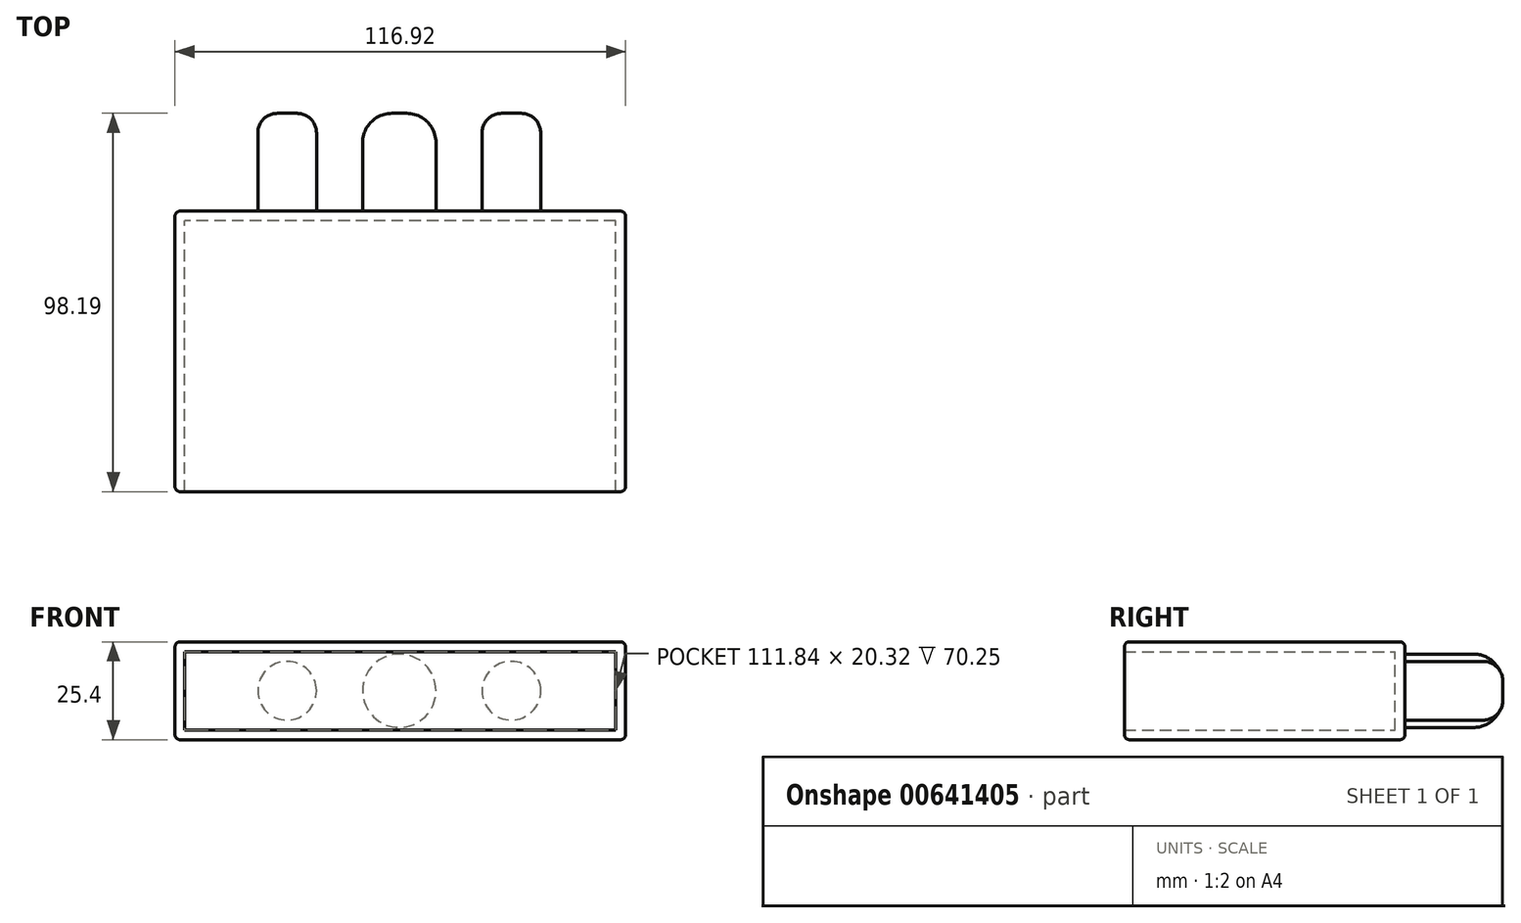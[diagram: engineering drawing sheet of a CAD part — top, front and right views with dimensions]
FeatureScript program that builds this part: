
annotation { "Feature Type Name" : "Feature", "Feature Type Description" : "" }
export const myFeature = defineFeature(function(context is Context, id is Id, definition is map)
    precondition{}
    {
        {
            var Q0;
            Q0=qCreatedBy(makeId("Top.planeOp"),FACE);
            var sketch = newSketch(context, id + "F0", { "sketchPlane" : qUnion([Q0])});
            skLineSegment(sketch, "E0.bottom", {"start": v(-58.2, 31.02) * mm, "end": v(58.72, 31.02) * mm});
            skLineSegment(sketch, "E0.top", {"start": v(-58.2, -41.77) * mm, "end": v(58.72, -41.77) * mm});
            skLineSegment(sketch, "E0.left", {"start": v(-58.2, 31.02) * mm, "end": v(-58.2, -41.77) * mm});
            skLineSegment(sketch, "E0.right", {"start": v(58.72, 31.02) * mm, "end": v(58.72, -41.77) * mm});
            skSolve(sketch);
        }
        {
            var Q0;
            Q0 = qSketchRegion(id + "F0", true);
            extrude(context, id + "F1", {"entities" : qUnion([Q0]), "depth" : 25.4 * mm, "offsetDistance" : 25.4 * mm});
        }
        {
            var Q0;
            Q0=makeQuery(id+"F1.opExtrude","SWEPT_FACE",FACE,{"disambiguationData":[OSD([sQuery(id+"F0.wireOp",EDGE,"E0.bottom")])]});
            var sketch = newSketch(context, id + "F2", { "sketchPlane" : qUnion([Q0])});
            skCircle(sketch, "E1", {"center": v(0, 12.7) * mm, "radius": 9.53 * mm});
            skLineSegment(sketch, "E2", {"start": v(0, 12.7) * mm, "end": v(0, 0) * mm, "construction": true});
            skLineSegment(sketch, "E3", {"start": v(0, 12.7) * mm, "end": v(58.2, 12.7) * mm, "construction": true});
            skCircle(sketch, "E4", {"center": v(29.1, 12.7) * mm, "radius": 7.62 * mm});
            skCircle(sketch, "E5.MirrorC", {"center": v(-29.1, 12.7) * mm, "radius": 7.62 * mm});
            skSolve(sketch);
        }
        {
            var Q0;
            Q0 = qSketchRegion(id + "F2", true);
            var Q1;
            Q1=sQuery(id+"F2.wireOp",EDGE,"E1");
            extrude(context, id + "F3", {"entities" : qUnion([Q0]), "surfaceEntities" : qUnion([Q1]), "depth" : 25.4 * mm, "offsetDistance" : 25.4 * mm});
        }
        {
            var Q0;
            Q0=makeQuery(id+"F3.opExtrude","CAP_EDGE",EDGE,{"disambiguationData":[OSD([sQuery(id+"F2.wireOp",EDGE,"E4")])],"isStart":false});
            var Q1;
            Q1=makeQuery(id+"F3.opExtrude","CAP_EDGE",EDGE,{"disambiguationData":[OSD([sQuery(id+"F2.wireOp",EDGE,"E5.MirrorC")])],"isStart":false});
            fillet(context, id + "F4", {"entities" : qUnion([Q0, Q1]), "radius" : 5.08 * mm, "tangentPropagation" : true, "allowEdgeOverflow" : false});
        }
        {
            var Q0;
            Q0=makeQuery(id+"F3.opExtrude","CAP_EDGE",EDGE,{"disambiguationData":[OSD([sQuery(id+"F2.wireOp",EDGE,"E1")])],"isStart":false});
            fillet(context, id + "F5", {"entities" : qUnion([Q0]), "radius" : 7.62 * mm, "tangentPropagation" : true, "allowEdgeOverflow" : false});
        }
        {
            var Q0;
            Q0=makeQuery(id+"F1.opExtrude","CAP_FACE",FACE,{"disambiguationData":[OSD([sQuery(id+"F0.wireOp",EDGE,"E0.bottom"),sQuery(id+"F0.wireOp",EDGE,"E0.top"),sQuery(id+"F0.wireOp",EDGE,"E0.left"),sQuery(id+"F0.wireOp",EDGE,"E0.right")])],"isStart":false});
            var Q1;
            Q1=makeQuery(id+"F1.opExtrude","SWEPT_FACE",FACE,{"disambiguationData":[OSD([sQuery(id+"F0.wireOp",EDGE,"E0.left")])]});
            var Q2;
            Q2=makeQuery(id+"F1.opExtrude","SWEPT_FACE",FACE,{"disambiguationData":[OSD([sQuery(id+"F0.wireOp",EDGE,"E0.right")])]});
            var Q3;
            Q3=makeQuery(id+"F1.opExtrude","CAP_FACE",FACE,{"disambiguationData":[OSD([sQuery(id+"F0.wireOp",EDGE,"E0.bottom"),sQuery(id+"F0.wireOp",EDGE,"E0.top"),sQuery(id+"F0.wireOp",EDGE,"E0.left"),sQuery(id+"F0.wireOp",EDGE,"E0.right")])],"isStart":true});
            fillet(context, id + "F6", {"entities" : qUnion([Q0, Q1, Q2, Q3]), "radius" : 1.27 * mm, "tangentPropagation" : true, "allowEdgeOverflow" : false});
        }
        {
            var Q0;
            Q0=makeQuery(id+"F1.opExtrude","SWEPT_FACE",FACE,{"disambiguationData":[OSD([sQuery(id+"F0.wireOp",EDGE,"E0.top")])]});
            shell(context, id + "F7", {"entities" : qUnion([Q0]), "thickness" : 2.54 * mm});
        }
    });
